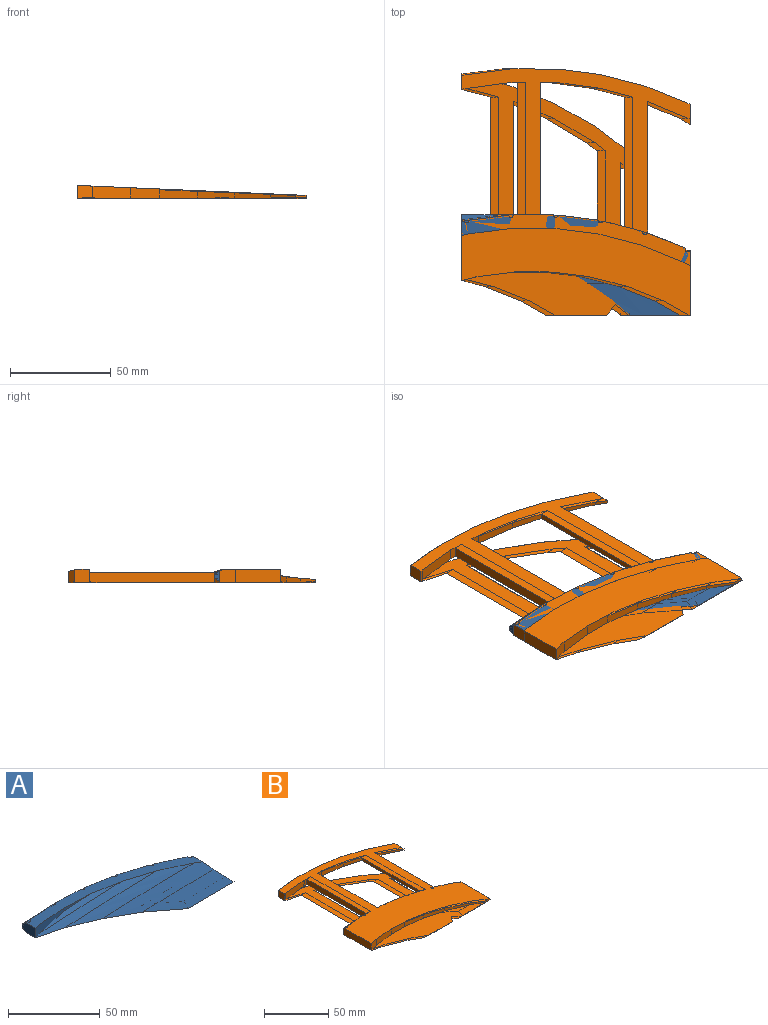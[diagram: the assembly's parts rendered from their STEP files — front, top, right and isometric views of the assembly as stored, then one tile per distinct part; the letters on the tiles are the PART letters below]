
ASSEMBLY  parts=2 mates=1
PART A: 70 faces, bbox 155.7x53x99.2 mm
  f0: revolved ~1.28x0.29mm, area 0.2mm2, adj f17,f42,f69
  f1: plane 1.03x0.27mm, normal (-0.25,-0.97,0), area 0.1mm2, adj f14,f47
  f2: plane 21.42x1.97mm, normal (0,-1,0), area 20.6mm2, adj f4,f8,f56
  f3: plane 21.42x1.7mm, normal (0,-1,0), area 25.9mm2, adj f14,f15,f52,f67
  f4: plane 21.37x5.92mm, normal (0.13,-0.99,0), area 84.6mm2, adj f2,f8,f16,f56
  f5: bspline ~92.22x2.73mm, area 0.4mm2, adj f6,f48,f49,f51,f67
  f6: plane 19.91x3.27mm, normal (-0.13,0.99,0), area 37.2mm2, adj f5,f7,f55,f67
  f7: bspline ~92.21x2.43mm, area 12.1mm2, adj f6,f21,f54,f57,f58,f67
  f8: plane 113.9x25.93mm, normal (0.04,0,1), area 776.8mm2, adj f2,f4,f9,f10,f16,f18,f20,f21
  f9: plane 18.99x7.6mm, normal (0.37,0.93,0), area 42.7mm2, adj f8,f10,f26,f67
  f10: bspline ~92.26x3.52mm, area 6.7mm2, adj f8,f9,f65,f66,f67,f68
  f11: plane 4.09x2.3mm, normal (-0.49,-0.87,0), area 5.1mm2, adj f12,f34,f67,f68
  f12: plane 20.49x8.21mm, normal (-0.37,-0.93,0), area 31.2mm2, adj f11,f13,f33,f34,f46,f67
  f13: plane 21.23x5.48mm, normal (-0.25,-0.97,0), area 39.6mm2, adj f12,f14,f46,f67
  f14: plane 21.76x3.1mm, normal (-0.13,-0.99,0), area 39.7mm2, adj f1,f3,f13,f46,f47,f52,f67
  f15: plane 7.65x0.97mm, normal (0.13,-0.99,0), area 2.6mm2, adj f3,f52,f67
  f16: plane 6.52x3.5mm, normal (0.25,-0.97,0), area 22.5mm2, adj f4,f8,f41,f67,f69
  f17: plane 1.11x0.34mm, normal (-0.25,0.97,0), area 0.3mm2, adj f0,f18,f43,f69
  f18: bspline ~92.22x2.73mm, area 0.2mm2, adj f8,f17,f43
  f19: plane 8.53x1.08mm, normal (-0.13,0.99,0), area 3.8mm2, adj f20,f45
  f20: bspline ~92.21x2.43mm, area 0.2mm2, adj f8,f19,f45
  f21: plane 47.72x7.59mm, normal (0,1,0), area 146.2mm2, adj f7,f8,f22,f45,f54,f67,f69
  f22: bspline ~92.21x2.43mm, area 16mm2, adj f8,f21,f23,f31,f32,f67
  f23: plane 19.89x4.43mm, normal (0.13,0.99,0), area 80.2mm2, adj f8,f22,f24,f67
  f24: bspline ~92.22x2.73mm, area 12.7mm2, adj f8,f23,f25,f29,f30,f67
  f25: plane 19.8x5.11mm, normal (0.25,0.97,0), area 62mm2, adj f8,f24,f26,f67
  f26: bspline ~92.23x2.94mm, area 9.3mm2, adj f8,f9,f25,f27,f28,f67
  f27: revolved ~5.35x0.8mm, area 1.3mm2, adj f26,f28
  f28: revolved ~3.33x0.8mm, area 1.2mm2, adj f8,f26,f27
  f29: revolved ~3.45x0.95mm, area 1.4mm2, adj f8,f24,f30
  f30: revolved ~8.65x0.95mm, area 1.7mm2, adj f24,f29
  f31: revolved ~3.45x1.08mm, area 1.6mm2, adj f8,f22,f32
  f32: revolved ~18.28x1.08mm, area 2.3mm2, adj f22,f31
  f33: revolved ~58.88x1.89mm, area 145.3mm2, adj f12,f34,f46,f67
  f34: revolved ~75.25x10.28mm, area 570.8mm2, adj f11,f12,f33,f35,f67,f68
  f35: revolved ~55.15x2.05mm, area 138.6mm2, adj f34,f36,f67,f68
  f36: revolved ~68.34x13.73mm, area 566.4mm2, adj f35,f37,f67,f68
  f37: revolved ~37.43x6.64mm, area 222.4mm2, adj f36,f38,f67,f68
  f38: revolved ~75.28x15.47mm, area 695.8mm2, adj f37,f39,f67,f68
  f39: revolved ~90.63x11.15mm, area 721.6mm2, adj f8,f38,f40,f67,f68
  f40: revolved ~91.32x8.21mm, area 587.1mm2, adj f8,f39,f41,f67
  f41: revolved ~92.08x5.48mm, area 397.9mm2, adj f8,f16,f40,f56,f67
  f42: revolved ~2.18x0.28mm, area 0.2mm2, adj f0,f8,f69
  f43: revolved ~4.56x1.39mm, area 3mm2, adj f8,f17,f18,f44,f69
  f44: revolved ~43.18x2.51mm, area 43.4mm2, adj f8,f43,f45,f69
  f45: revolved ~28.29x2.3mm, area 63.9mm2, adj f8,f19,f20,f21,f44,f69
  f46: revolved ~71.59x7.6mm, area 377.5mm2, adj f12,f13,f14,f33,f47,f67
  f47: revolved ~50.97x2.12mm, area 104.8mm2, adj f1,f14,f46,f52,f67
  f48: revolved ~4.7x1.39mm, area 3.3mm2, adj f5,f55,f61,f62,f69
  f49: revolved ~3.45x0.95mm, area 1.4mm2, adj f5,f51,f61
  f50: revolved ~1.18x0.28mm, area 0.2mm2, adj f53,f62,f69
  f51: revolved ~7.65x0.89mm, area 1.4mm2, adj f5,f49,f63,f67
  f52: revolved ~44.14x1.93mm, area 46.8mm2, adj f3,f14,f15,f47,f67
  f53: revolved ~2.87x0.25mm, area 0.2mm2, adj f50,f64,f67,f69
  f54: revolved ~30.59x1.82mm, area 55.5mm2, adj f7,f21,f55,f59,f60,f69
  f55: revolved ~63.08x3.03mm, area 39.7mm2, adj f6,f48,f54,f69
  f56: revolved ~85.49x4.03mm, area 135.6mm2, adj f2,f4,f8,f41
  f57: revolved ~3.45x1.08mm, area 1.6mm2, adj f7,f58,f59
  f58: revolved ~18.29x1.08mm, area 2.3mm2, adj f7,f57
  f59: bspline ~92.21x2.43mm, area 0.2mm2, adj f54,f57,f60
  f60: plane 8.92x1.47mm, normal (-0.13,0.99,0), area 1.4mm2, adj f54,f59
  f61: bspline ~92.22x2.73mm, area 0.2mm2, adj f48,f49,f62
  f62: plane 1.11x0.3mm, normal (-0.25,0.97,0), area 0.2mm2, adj f48,f50,f61,f69
  f63: bspline ~92.22x2.73mm, area 0mm2, adj f51,f64,f67
  f64: plane 0.96x0.25mm, normal (-0.25,0.97,0), area 0.1mm2, adj f53,f63,f67
  f65: revolved ~4.21x0.75mm, area 1.3mm2, adj f10,f66
  f66: revolved ~3.58x0.75mm, area 1.2mm2, adj f8,f10,f65
  f67: plane 113.81x50.16mm, normal (0,0,-1), area 1323.4mm2, adj f3,f5,f6,f7,f9,f10,f11,f12
  f68: plane 32.11x1.58mm, normal (1,0,0), area 19.7mm2, adj f8,f10,f11,f34,f35,f36,f37,f38
  f69: plane 12.57x8.7mm, normal (-1,0,0), area 60.3mm2, adj f0,f8,f16,f17,f21,f42,f43,f44
PART B: 118 faces, bbox 121.3x122.7x97.5 mm
  f0: revolved ~4.8x0.7mm, area 1.1mm2, adj f1,f17
  f1: cylinder r=1624.31mm len=2.28mm, axis (0,-1,0), area 1.1mm2, adj f0,f17,f18
  f2: revolved ~8.03x3.15mm, area 4.5mm2, adj f7,f21,f22,f26
  f3: revolved ~8.35x0.52mm, area 1mm2, adj f37,f38,f50,f51
  f4: plane 3.23x1.2mm, normal (0.25,0.97,0), area 4mm2, adj f5,f6,f36,f53
  f5: revolved ~7.71x0.89mm, area 1.4mm2, adj f4,f6,f53,f54
  f6: bspline ~92.22x2.73mm, area 4.1mm2, adj f4,f5,f36,f55
  f7: plane 63.36x41.4mm, normal (0,0,1), area 573.4mm2, adj f2,f21,f26,f27,f28,f29,f34,f35
  f8: revolved ~4.21x0.75mm, area 1.3mm2, adj f78,f79
  f9: plane 12.57x7.07mm, normal (-0.49,-0.87,0), area 22.3mm2, adj f10,f13,f14,f81,f82
  f10: plane 17.9x7.18mm, normal (-0.37,-0.93,0), area 43.8mm2, adj f9,f12,f13,f83
  f11: plane 18.65x4.23mm, normal (-0.13,-0.99,0), area 71.8mm2, adj f12,f85,f86,f92
  f12: plane 18.55x4.79mm, normal (-0.25,-0.97,0), area 59.4mm2, adj f10,f11,f13,f84,f92
  f13: revolved ~22.28x8.54mm, area 53.3mm2, adj f9,f10,f12,f14,f92
  f14: revolved ~28.09x6.64mm, area 121.2mm2, adj f9,f13,f81,f92
  f15: bspline ~92.2x2.43mm, area 2mm2, adj f16,f64,f65,f97
  f16: plane 5.27x4.11mm, normal (-0.13,0.99,0), area 11.1mm2, adj f15,f63,f64,f89,f97,f98
  f17: bspline ~92.23x2.94mm, area 8.9mm2, adj f0,f1,f18,f114
  f18: plane 2.49x2.22mm, normal (-0.31,-0.95,0), area 5.8mm2, adj f1,f17,f114
  f19: plane 56.3x0.24mm, normal (1,0,0), area 13.1mm2, adj f20,f65,f97,f114
  f20: revolved ~10.37x2.56mm, area 3.4mm2, adj f19,f31,f97,f114
  f21: plane 31.31x0.1mm, normal (1,0,0), area 2.9mm2, adj f2,f7,f22,f55,f114
  f22: revolved ~3.15x2.47mm, area 3.3mm2, adj f2,f21,f23,f26,f114
  f23: plane 0.97x0.76mm, normal (-0.62,-0.79,0), area 0mm2, adj f22,f26,f114
  f24: plane 21.17x4.29mm, normal (-0.13,-0.99,0), area 81.6mm2, adj f25,f58,f59,f114
  f25: plane 16.04x4.31mm, normal (-0.26,-0.97,0), area 50.9mm2, adj f24,f26,f57,f114
  f26: plane 64.33x2.73mm, normal (-1,0,0), area 175mm2, adj f2,f7,f22,f23,f25,f27,f55,f56
  f27: plane 14.36x10.83mm, normal (0.6,0.8,0), area 2mm2, adj f7,f26,f28,f114
  f28: plane 20.62x11.57mm, normal (0.49,0.87,0), area 3.7mm2, adj f7,f27,f29,f114
  f29: plane 6.42x2.57mm, normal (0.37,0.93,0), area 1.3mm2, adj f7,f28,f48,f114
  f30: plane 5.07x0.12mm, normal (0,-1,0), area 0.5mm2, adj f67,f94,f114
  f31: plane 65.7x4.91mm, normal (-1,0,0), area 320.8mm2, adj f20,f32,f65,f66,f67,f97,f114
  f32: plane 3.24x1.3mm, normal (0.37,0.93,0), area 0.8mm2, adj f31,f33,f97,f114
  f33: plane 4.46x1.15mm, normal (0.25,0.97,0), area 1.1mm2, adj f32,f94,f97,f114
  f34: revolved ~24.87x12.18mm, area 51.9mm2, adj f7,f35,f39,f114
  f35: revolved ~9.38x4.02mm, area 17.1mm2, adj f7,f34,f36,f114
  f36: cylinder r=1622.35mm len=35.73mm, axis (0,-1,0), area 149.2mm2, adj f4,f6,f7,f35,f52,f53,f55,f114
  f37: bspline ~92.21x2.43mm, area 2.3mm2, adj f3,f38,f52,f114
  f38: plane 4.17x2.09mm, normal (0.13,0.99,0), area 8.7mm2, adj f3,f37,f50,f114
  f39: revolved ~10.67x2.69mm, area 7.7mm2, adj f7,f34,f48,f114
  f40: revolved ~22.17x7.18mm, area 30.8mm2, adj f41,f92,f93,f114
  f41: revolved ~16.82x7.07mm, area 30.1mm2, adj f40,f42,f92,f114
  f42: plane 30.33x0.18mm, normal (0,-1,0), area 4.3mm2, adj f41,f43,f92,f114
  f43: plane 5.09x4.1mm, normal (0.78,-0.63,0), area 0.6mm2, adj f42,f44,f92,f114
  f44: revolved ~10.91x5.09mm, area 17.4mm2, adj f43,f81,f92,f114
  f45: plane 15.68x6.57mm, normal (-0.39,-0.92,0), area 32.9mm2, adj f46,f75,f76,f114
  f46: plane 5.44x3.22mm, normal (-0.51,-0.86,0), area 9.5mm2, adj f45,f73,f74,f114
  f47: plane 5.07x0.13mm, normal (-0.13,0.99,0), area 0.5mm2, adj f68,f87,f90,f114
  f48: plane 65.67x4.81mm, normal (1,0,0), area 314.2mm2, adj f7,f29,f39,f49,f59,f113,f114
  f49: plane 6.29x4.81mm, normal (0,1,0), area 29.4mm2, adj f48,f50,f113,f114
  f50: bspline ~92.21x2.43mm, area 1.9mm2, adj f3,f38,f49,f51,f113,f114
  f51: revolved ~3.45x1.08mm, area 1.6mm2, adj f3,f50,f113
  f52: plane 19.89x4.43mm, normal (0.13,0.99,0), area 80.2mm2, adj f36,f37,f53,f113,f114
  f53: bspline ~92.22x2.73mm, area 3.9mm2, adj f4,f5,f36,f52,f54,f113
  f54: revolved ~3.45x0.95mm, area 1.4mm2, adj f5,f53,f113
  f55: plane 14.89x3.84mm, normal (0.25,0.97,0), area 35.1mm2, adj f6,f7,f21,f26,f36,f56,f113,f114
  f56: cylinder r=1624.75mm len=65.43mm, axis (0,-1,0), area 276mm2, adj f26,f55,f57,f113
  f57: revolved ~20.29x4.31mm, area 18.9mm2, adj f25,f56,f58,f113
  f58: revolved ~25.44x2.84mm, area 13.9mm2, adj f24,f57,f59,f113
  f59: plane 8.5x4.84mm, normal (0,-1,0), area 20.7mm2, adj f24,f48,f58,f113,f114
  f60: bspline ~92.23x2.94mm, area 0.1mm2, adj f61,f62,f113
  f61: revolved ~3.33x0.8mm, area 1.2mm2, adj f60,f62,f113
  f62: revolved ~4.45x0.73mm, area 0.8mm2, adj f60,f61,f113
  f63: bspline ~92.21x2.43mm, area 0.2mm2, adj f16,f64,f113
  f64: revolved ~5.41x1.22mm, area 2.8mm2, adj f15,f16,f63,f65,f113
  f65: plane 10.55x5.41mm, normal (0,1,0), area 33.2mm2, adj f15,f19,f31,f64,f66,f97,f113,f114
  f66: cylinder r=1628.88mm len=65.7mm, axis (0,-1,0), area 280.1mm2, adj f31,f65,f67,f113
  f67: plane 7.46x5.48mm, normal (0,-1,0), area 18mm2, adj f30,f31,f66,f94,f113,f114
  f68: plane 23.44x5.48mm, normal (0,1,0), area 115.8mm2, adj f47,f69,f90,f113,f114
  f69: plane 21.04x4.43mm, normal (0.13,0.99,0), area 84.3mm2, adj f68,f70,f113,f114
  f70: plane 22.06x5.69mm, normal (0.25,0.97,0), area 69.1mm2, adj f69,f71,f113,f114
  f71: plane 21.3x8.53mm, normal (0.37,0.93,0), area 47.9mm2, adj f70,f72,f113,f114
  f72: plane 1.62x1.19mm, normal (0.49,0.87,0), area 2.2mm2, adj f71,f73,f113,f114
  f73: plane 10.02x1.57mm, normal (1,0,0), area 15.5mm2, adj f46,f72,f74,f113,f114
  f74: revolved ~9.69x3.22mm, area 8.4mm2, adj f46,f73,f75,f113
  f75: revolved ~24.18x8.35mm, area 31.9mm2, adj f45,f74,f76,f113
  f76: plane 65.34x2.49mm, normal (1,0,0), area 158.7mm2, adj f45,f75,f77,f113,f114
  f77: plane 18.73x7.5mm, normal (0.37,0.93,0), area 42.1mm2, adj f76,f78,f113,f114
  f78: bspline ~92.26x3.52mm, area 6.7mm2, adj f8,f77,f79,f80,f113,f114
  f79: revolved ~3.58x0.75mm, area 1.2mm2, adj f8,f78,f113
  f80: plane 32.11x1.57mm, normal (1,0,0), area 50.4mm2, adj f78,f81,f113,f114
  f81: plane 34.81x1.61mm, normal (0,-1,0), area 15.1mm2, adj f9,f14,f44,f80,f82,f113,f114
  f82: revolved ~16.82x7.07mm, area 30.1mm2, adj f9,f81,f83,f113
  f83: revolved ~22.16x7.18mm, area 30.8mm2, adj f10,f82,f84,f113
  f84: revolved ~22.8x4.79mm, area 21.1mm2, adj f12,f83,f85,f113
  f85: revolved ~22.91x2.35mm, area 11.9mm2, adj f11,f84,f86,f113
  f86: plane 18.72x5.18mm, normal (0,-1,0), area 70.9mm2, adj f11,f85,f91,f92,f113
  f87: plane 5.22x4.16mm, normal (0,1,0), area 21.3mm2, adj f47,f90,f110,f114
  f88: bspline ~92.22x2.73mm, area 0.2mm2, adj f101,f104,f113
  f89: revolved ~4.42x0.52mm, area 1.1mm2, adj f16,f98,f100
  f90: revolved ~8.51x0.41mm, area 0.9mm2, adj f47,f68,f87,f108
  f91: plane 18.65x5.96mm, normal (0.13,-0.99,0), area 103.9mm2, adj f86,f92,f112,f113
  f92: plane 83.23x21.38mm, normal (0,0,1), area 1055mm2, adj f11,f12,f13,f14,f40,f41,f42,f43
  f93: revolved ~17.51x3.42mm, area 13.8mm2, adj f40,f92,f112,f114
  f94: plane 23.36x6.5mm, normal (0.13,-0.99,0), area 134.9mm2, adj f30,f33,f67,f95,f97,f107,f113,f114
  f95: revolved ~20.12x4.26mm, area 17.7mm2, adj f94,f96,f97,f107,f114
  f96: cylinder r=1624.75mm len=59.26mm, axis (0,-1,0), area 250.9mm2, adj f95,f97,f99,f114
  f97: plane 65.82x25.2mm, normal (0,0,1), area 542.6mm2, adj f15,f16,f19,f20,f31,f32,f33,f65
  f98: bspline ~92.2x2.43mm, area 2.7mm2, adj f16,f89,f97,f99
  f99: plane 19.02x6.04mm, normal (-0.13,0.99,0), area 107.6mm2, adj f96,f97,f98,f100,f105,f106,f114,f116
  f100: revolved ~24.15x2.51mm, area 13.9mm2, adj f89,f99,f101,f113,f116
  f101: revolved ~4.56x1.39mm, area 3mm2, adj f88,f100,f104,f113,f116
  f102: revolved ~1.28x0.29mm, area 0.2mm2, adj f103,f104,f116
  f103: revolved ~2.18x0.28mm, area 0.2mm2, adj f102,f113,f116
  f104: plane 1.11x0.34mm, normal (-0.25,0.97,0), area 0.3mm2, adj f88,f101,f102,f116
  f105: plane 0.3x0.13mm, normal (0.13,0.99,0), area 0mm2, adj f99,f106,f114,f116
  f106: plane 0.13x0.03mm, normal (0,0,1), area 0mm2, adj f99,f105,f116
  f107: plane 6.52x1.09mm, normal (0.26,-0.96,0), area 7.3mm2, adj f94,f95,f113,f117
  f108: revolved ~27.6x3.02mm, area 15.8mm2, adj f90,f109,f110,f113,f117
  f109: revolved ~2.18x0.29mm, area 0.2mm2, adj f108,f113,f117
  f110: plane 20.17x6.04mm, normal (-0.13,0.99,0), area 114.4mm2, adj f87,f108,f111,f114,f115,f117
  f111: plane 0.41x0.3mm, normal (0.13,0.99,0), area 0.1mm2, adj f110,f114,f115,f117
  f112: plane 7.55x6.52mm, normal (0.25,-0.97,0), area 47.7mm2, adj f91,f92,f93,f113,f114,f116
  f113: plane 122.7x113.9mm, normal (0.04,0,1), area 5071.3mm2, adj f48,f49,f50,f51,f52,f53,f54,f55
  f114: plane 122.6x113.81mm, normal (0,0,-1), area 8747.6mm2, adj f17,f18,f19,f20,f21,f22,f23,f24
  f115: plane 0.41x0.11mm, normal (0,0,1), area 0mm2, adj f110,f111,f117
  f116: plane 30.31x6.64mm, normal (-1,0,0), area 196.4mm2, adj f99,f100,f101,f102,f103,f104,f105,f106
  f117: plane 7.67x6.52mm, normal (-1,0,0), area 49.2mm2, adj f107,f108,f109,f110,f111,f113,f114,f115
PLACE A at identity
PLACE B at identity
MATE fastened B.f114 <-> A.f67  axis (0,0,-1) through (375.41,-242.11,188.35)mm
